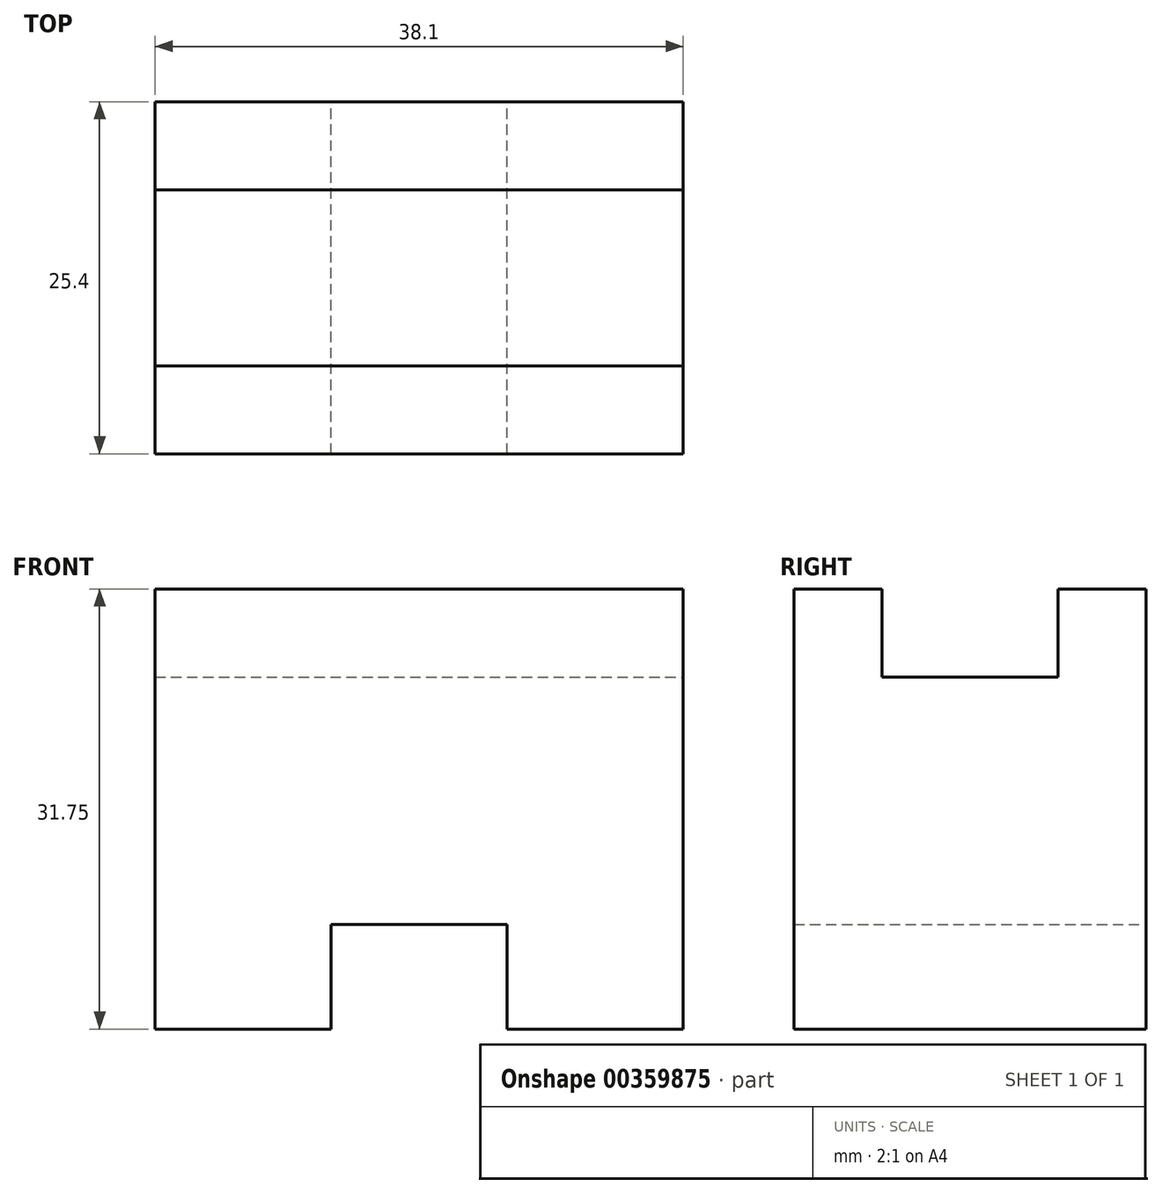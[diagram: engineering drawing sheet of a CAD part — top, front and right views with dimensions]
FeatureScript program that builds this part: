
annotation { "Feature Type Name" : "Feature", "Feature Type Description" : "" }
export const myFeature = defineFeature(function(context is Context, id is Id, definition is map)
    precondition{}
    {
        {
            var Q0;
            Q0=qCreatedBy(makeId("Front.planeOp"),FACE);
            var sketch = newSketch(context, id + "F0", { "sketchPlane" : qUnion([Q0])});
            skLineSegment(sketch, "E0", {"start": v(0, 0) * mm, "end": v(12.7, 0) * mm});
            skLineSegment(sketch, "E1", {"start": v(12.7, 0) * mm, "end": v(12.7, 7.54) * mm});
            skLineSegment(sketch, "E2", {"start": v(12.7, 7.54) * mm, "end": v(25.4, 7.54) * mm});
            skLineSegment(sketch, "E3", {"start": v(25.4, 7.54) * mm, "end": v(25.4, 0) * mm});
            skLineSegment(sketch, "E4", {"start": v(25.4, 0) * mm, "end": v(38.1, 0) * mm});
            skLineSegment(sketch, "E5", {"start": v(38.1, 0) * mm, "end": v(38.1, 31.75) * mm});
            skLineSegment(sketch, "E6", {"start": v(38.1, 31.75) * mm, "end": v(0, 31.75) * mm});
            skLineSegment(sketch, "E7", {"start": v(0, 31.75) * mm, "end": v(0, 0) * mm});
            skSolve(sketch);
        }
        {
            var Q0;
            Q0=makeQuery(id+"F0.imprint","IMPRINT",FACE,{"disambiguationData":[TD([[makeQuery(id+"F0.imprint","IMPRINT",EDGE,{"derivedFrom":sQuery(id+"F0.wireOp",EDGE,"E0")}),1.0]])]});
            extrude(context, id + "F1", {"entities" : qUnion([Q0]), "depth" : 25.4 * mm});
        }
        {
            var Q0;
            Q0=makeQuery(id+"F1.opExtrude","SWEPT_FACE",FACE,{"disambiguationData":[OSD([sQuery(id+"F0.wireOp",EDGE,"E5")])]});
            var sketch = newSketch(context, id + "F2", { "sketchPlane" : qUnion([Q0])});
            skLineSegment(sketch, "E8", {"start": v(-19.05, 31.75) * mm, "end": v(-19.05, 25.4) * mm});
            skLineSegment(sketch, "E9", {"start": v(-19.05, 25.4) * mm, "end": v(-6.35, 25.4) * mm});
            skLineSegment(sketch, "E10", {"start": v(-6.35, 25.4) * mm, "end": v(-6.35, 31.75) * mm});
            skSolve(sketch);
        }
        {
            var Q0;
            Q0 = qSketchRegion(id + "F2", true);
            var Q1;
            {var subQ0=sQuery(id+"F2.wireOp",EDGE,"E8");Q1=makeQuery(id+"F2.imprint","IMPRINT",FACE,{"disambiguationData":[TD([[makeQuery(id+"F2.imprint","IMPRINT",EDGE,{"derivedFrom":subQ0}),1.0]])]});}
            extrude(context, id + "F3", {"entities" : qUnion([Q0, Q1]), "operationType" : NewBodyOperationType.REMOVE, "oppositeDirection" : true, "depth" : 38.1 * mm});
        }
    });
